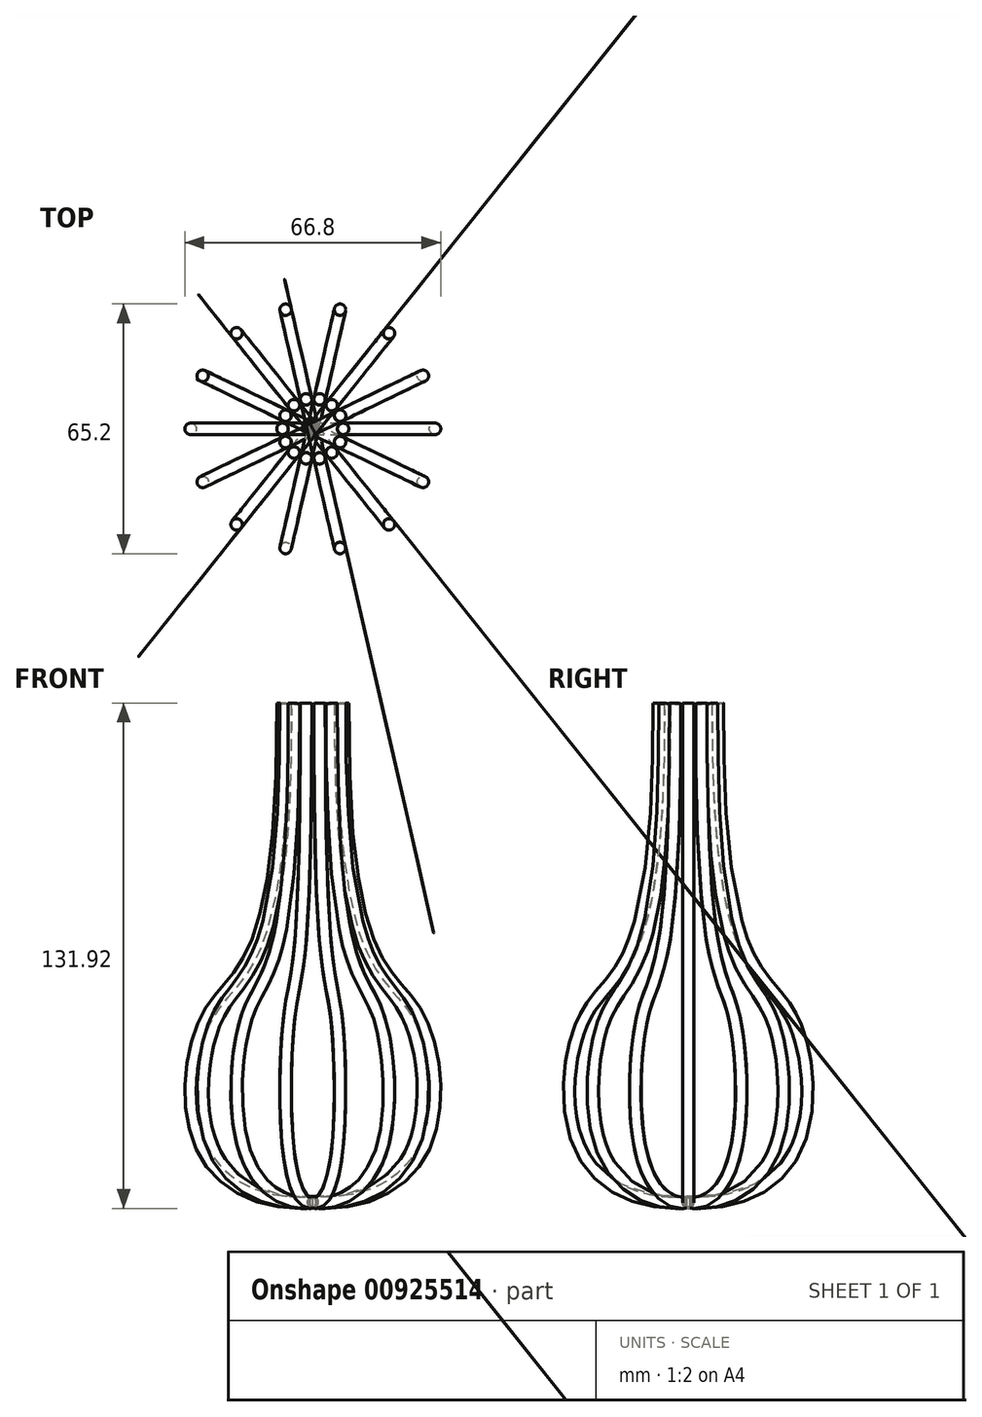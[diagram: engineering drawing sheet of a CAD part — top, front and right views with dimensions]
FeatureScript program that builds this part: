
annotation { "Feature Type Name" : "Feature", "Feature Type Description" : "" }
export const myFeature = defineFeature(function(context is Context, id is Id, definition is map)
    precondition{}
    {
        {
            var Q0;
            Q0=qCreatedBy(makeId("Front.planeOp"),FACE);
            var sketch = newSketch(context, id + "F0", { "sketchPlane" : qUnion([Q0])});
            skFitSpline(sketch, "E0", {"points": [v(8.01, 81.82) * mm, v(27.77, 0) * mm, v(29.07, -34.26) * mm, v(0, -48.46) * mm], "startDerivative": vector(-3.13, -493.8) * mm, "endDerivative": vector(-143.74, 11.65) * mm});
            skSolve(sketch);
        }
        {
            var Q0;
            Q0=qCreatedBy(makeId("Right.planeOp"),FACE);
            var sketch = newSketch(context, id + "F1", { "sketchPlane" : qUnion([Q0])});
            skCircle(sketch, "E1", {"center": v(0, -48.35) * mm, "radius": 1.5 * mm});
            skLineSegment(sketch, "E2", {"start": v(0, -48.35) * mm, "end": v(0, 0) * mm, "construction": true});
            skSolve(sketch);
        }
        {
            var Q0;
            Q0=makeQuery(id+"F1.imprint","IMPRINT",FACE,{"disambiguationData":[TD([[makeQuery(id+"F1.imprint","IMPRINT",EDGE,{"derivedFrom":sQuery(id+"F1.wireOp",EDGE,"E1")}),1.0]])]});
            var Q1;
            Q1=sQuery(id+"F0.wireOp",EDGE,"E0");
            sweep(context, id + "F2", {"profiles" : qUnion([Q0]), "path" : qUnion([Q1])});
        }
        {
            var Q0;
            Q0=makeQuery(id+"F2.opSweep","SWEPT_BODY",BODY,{"disambiguationData":[OSD([sQuery(id+"F0.wireOp",EDGE,"E0"),sQuery(id+"F1.wireOp",EDGE,"E1")])]});
            var Q1;
            Q1=qCreatedBy(makeId("Right.planeOp"),FACE);
            mirror(context, id + "F3", {"operationType" : NewBodyOperationType.ADD, "entities" : qUnion([Q0]), "mirrorPlane" : qUnion([Q1])});
        }
        {
            var Q0;
            Q0=qCreatedBy(makeId("Front.planeOp"),FACE);
            var sketch = newSketch(context, id + "F4", { "sketchPlane" : qUnion([Q0])});
            skLineSegment(sketch, "E3", {"start": v(0, 0) * mm, "end": v(0, 86.01) * mm, "construction": true});
            skSolve(sketch);
        }
        {
            var Q0;
            Q0=makeQuery(id+"F2.opSweep","SWEPT_BODY",BODY,{"disambiguationData":[OSD([sQuery(id+"F0.wireOp",EDGE,"E0"),sQuery(id+"F1.wireOp",EDGE,"E1")])]});
            var Q1;
            Q1=sQuery(id+"F4.wireOp",EDGE,"E3");
            circularPattern(context, id + "F5", {"entities" : qUnion([Q0]), "axis" : qUnion([Q1]), "angle" : 360 * degree, "instanceCount" : 7, "equalSpace" : true});
        }
    });
